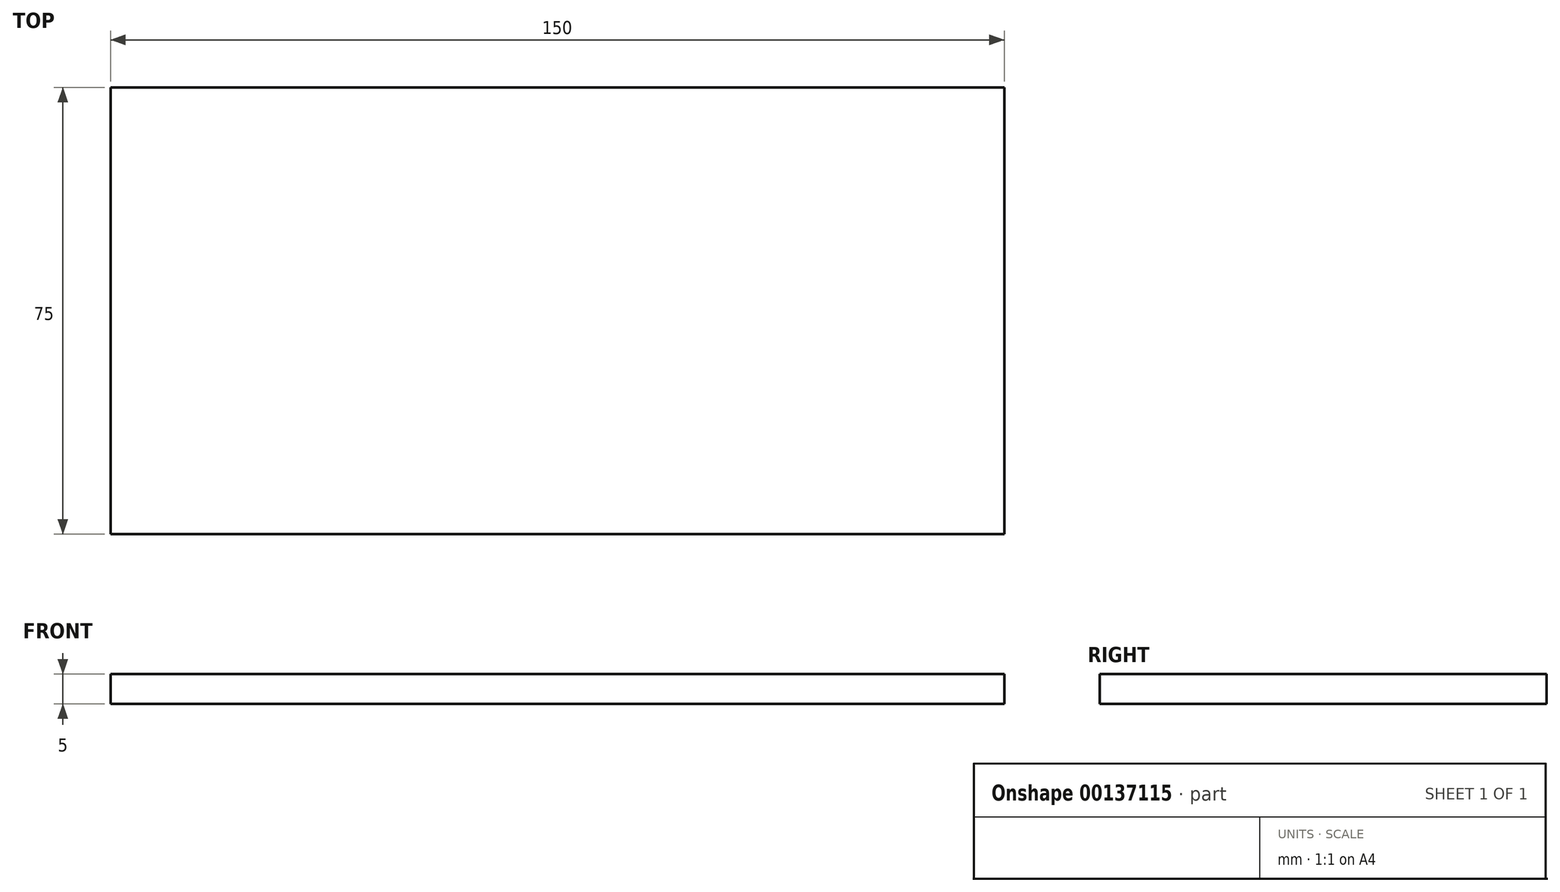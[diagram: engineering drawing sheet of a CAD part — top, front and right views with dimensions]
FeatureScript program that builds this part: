
annotation { "Feature Type Name" : "Feature", "Feature Type Description" : "" }
export const myFeature = defineFeature(function(context is Context, id is Id, definition is map)
    precondition{}
    {
        {
            var Q0;
            Q0=qCreatedBy(makeId("Top.planeOp"),FACE);
            var sketch = newSketch(context, id + "F0", { "sketchPlane" : qUnion([Q0])});
            skLineSegment(sketch, "E0.bottom", {"start": v(-73.17, 48.44) * mm, "end": v(76.83, 48.44) * mm});
            skLineSegment(sketch, "E0.top", {"start": v(-73.17, -26.56) * mm, "end": v(76.83, -26.56) * mm});
            skLineSegment(sketch, "E0.left", {"start": v(-73.17, 48.44) * mm, "end": v(-73.17, -26.56) * mm});
            skLineSegment(sketch, "E0.right", {"start": v(76.83, 48.44) * mm, "end": v(76.83, -26.56) * mm});
            skSolve(sketch);
        }
        {
            var Q0;
            Q0 = qSketchRegion(id + "F0", true);
            extrude(context, id + "F1", {"entities" : qUnion([Q0]), "depth" : 5 * mm});
        }
    });
